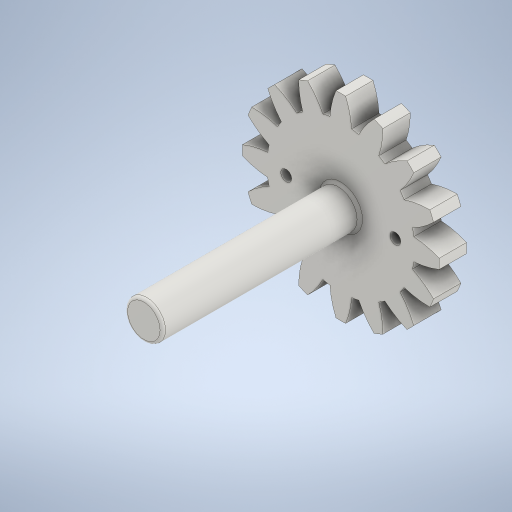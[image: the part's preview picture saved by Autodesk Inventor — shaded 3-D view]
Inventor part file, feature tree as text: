
AUTODESK INVENTOR PART (.ipt)
format: ipt  version: 2023.2 (Build 272271030, 271C)  size: 811,008 bytes
history: native  units: mm (DEFAULTED — no unit token found)
features: sketch x4, extrude x3, plane x3, other x3, fillet x1
ambient origin geometry x8: Origin, YZ Plane, XZ Plane, XY Plane, X Axis, Y Axis, Z Axis, Center Point
bodies: Solid1 (feature_tree)
feature tree (14):
  extrude  "Extrusion1"  Depth=5.0mm TaperAngle=0.0deg
  plane  "Work Plane2"
  plane  "Work Plane8"
  plane  "Work Plane9"
  other  "Spur Gear"
  extrude  "Extrusion2"  Depth=10.0mm TaperAngle=0.0deg
  fillet  "Fillet1"  Radius=24.0mm
  extrude  "Extrusion3"  TaperAngle=0.0deg  [1 undecoded]
  sketch  "Sketch1"  dims[d0=36.0mm d1=5.0mm d2=0.0mm]
  sketch  "Sketch2"  dims[d3=32.0mm d4=10.0mm d5=0.0mm d16=24.0mm]
  other  "Srf1"
  sketch  "Sketch3"  dims[d17=0.0mm d34=1.963495mm d39=0.0mm]
  sketch  "Sketch4"  dims[d41=0.0mm d43=24.0mm d46=24.0mm d47=0.0mm d48=0.0mm d49=6.95mm d50=36.0mm d51=0.0mm d52=0.5mm d53=9.97mm d54=2.0mm d55=40.0mm d56=0.0mm]
  other  "Pitch Diameter"
note: 1 required parameter value undecoded (feature->parameter linkage not recoverable at this tier; creation-order binding heuristic only, values carry confidence <= 0.55)
